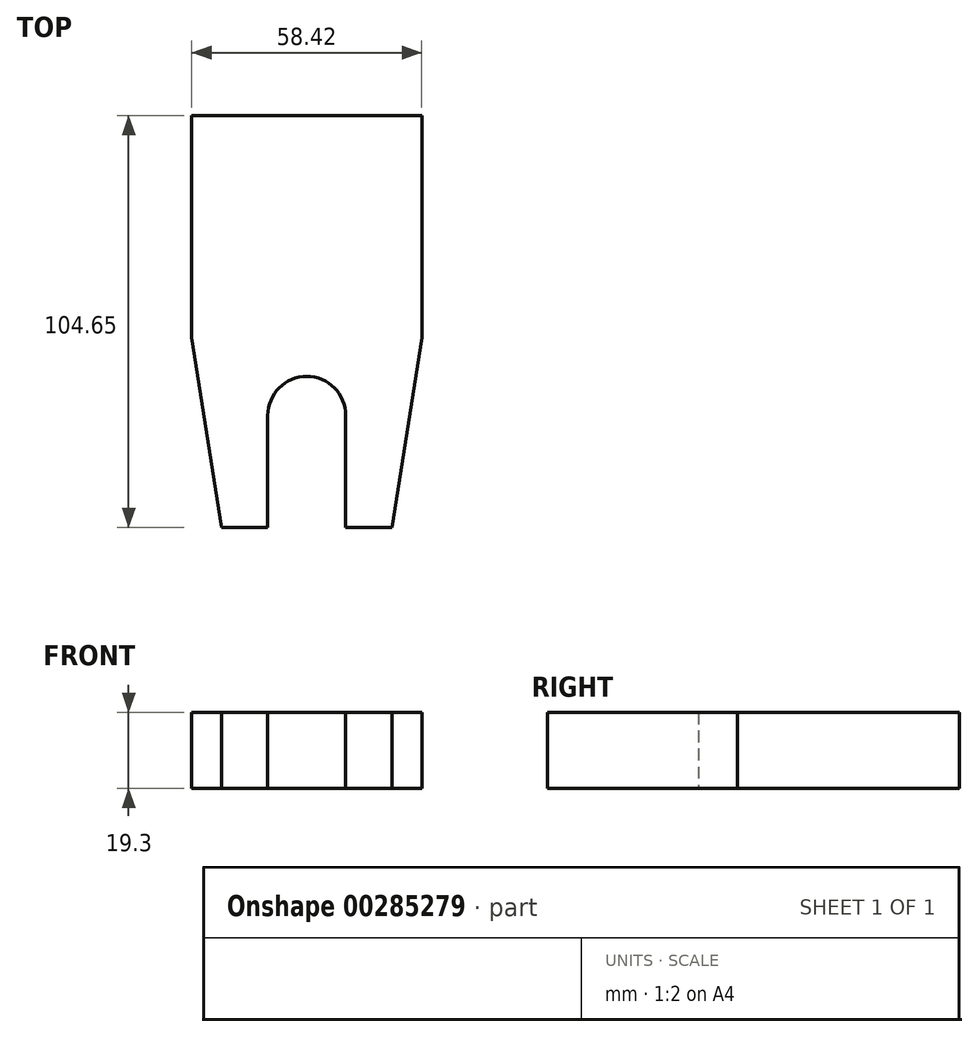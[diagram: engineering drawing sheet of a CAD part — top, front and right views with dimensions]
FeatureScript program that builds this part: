
annotation { "Feature Type Name" : "Feature", "Feature Type Description" : "" }
export const myFeature = defineFeature(function(context is Context, id is Id, definition is map)
    precondition{}
    {
        {
            var Q0;
            Q0=qCreatedBy(makeId("Top.planeOp"),FACE);
            var sketch = newSketch(context, id + "F0", { "sketchPlane" : qUnion([Q0])});
            skLineSegment(sketch, "E0.bottom", {"start": v(-16.53, 57.78) * mm, "end": v(41.9, 57.78) * mm});
            skLineSegment(sketch, "E0.top", {"start": v(-8.9, -46.87) * mm, "end": v(2.78, -46.87) * mm});
            skLineSegment(sketch, "E0.left", {"start": v(-16.53, 57.78) * mm, "end": v(-16.53, 1.4) * mm});
            skLineSegment(sketch, "E0.right", {"start": v(41.9, 57.78) * mm, "end": v(41.9, 1.4) * mm});
            skLineSegment(sketch, "E1.left", {"start": v(2.78, -18.42) * mm, "end": v(2.78, -46.87) * mm});
            skLineSegment(sketch, "E1.right", {"start": v(22.59, -18.42) * mm, "end": v(22.59, -46.87) * mm});
            skArc(sketch, "E2", {"start": v(22.59, -18.42) * mm, "mid": v(12.68, -8.52) * mm, "end": v(2.78, -18.42) * mm});
            skLineSegment(sketch, "E3", {"start": v(-8.9, -46.87) * mm, "end": v(-16.53, 1.4) * mm});
            skLineSegment(sketch, "E4", {"start": v(34.27, -46.87) * mm, "end": v(41.9, 1.4) * mm});
            skLineSegment(sketch, "E5.trimOffspring", {"start": v(22.59, -46.87) * mm, "end": v(34.27, -46.87) * mm});
            skSolve(sketch);
        }
        {
            var Q0;
            Q0 = qSketchRegion(id + "F0", true);
            extrude(context, id + "F1", {"entities" : qUnion([Q0]), "depth" : 19.3 * mm});
        }
    });
